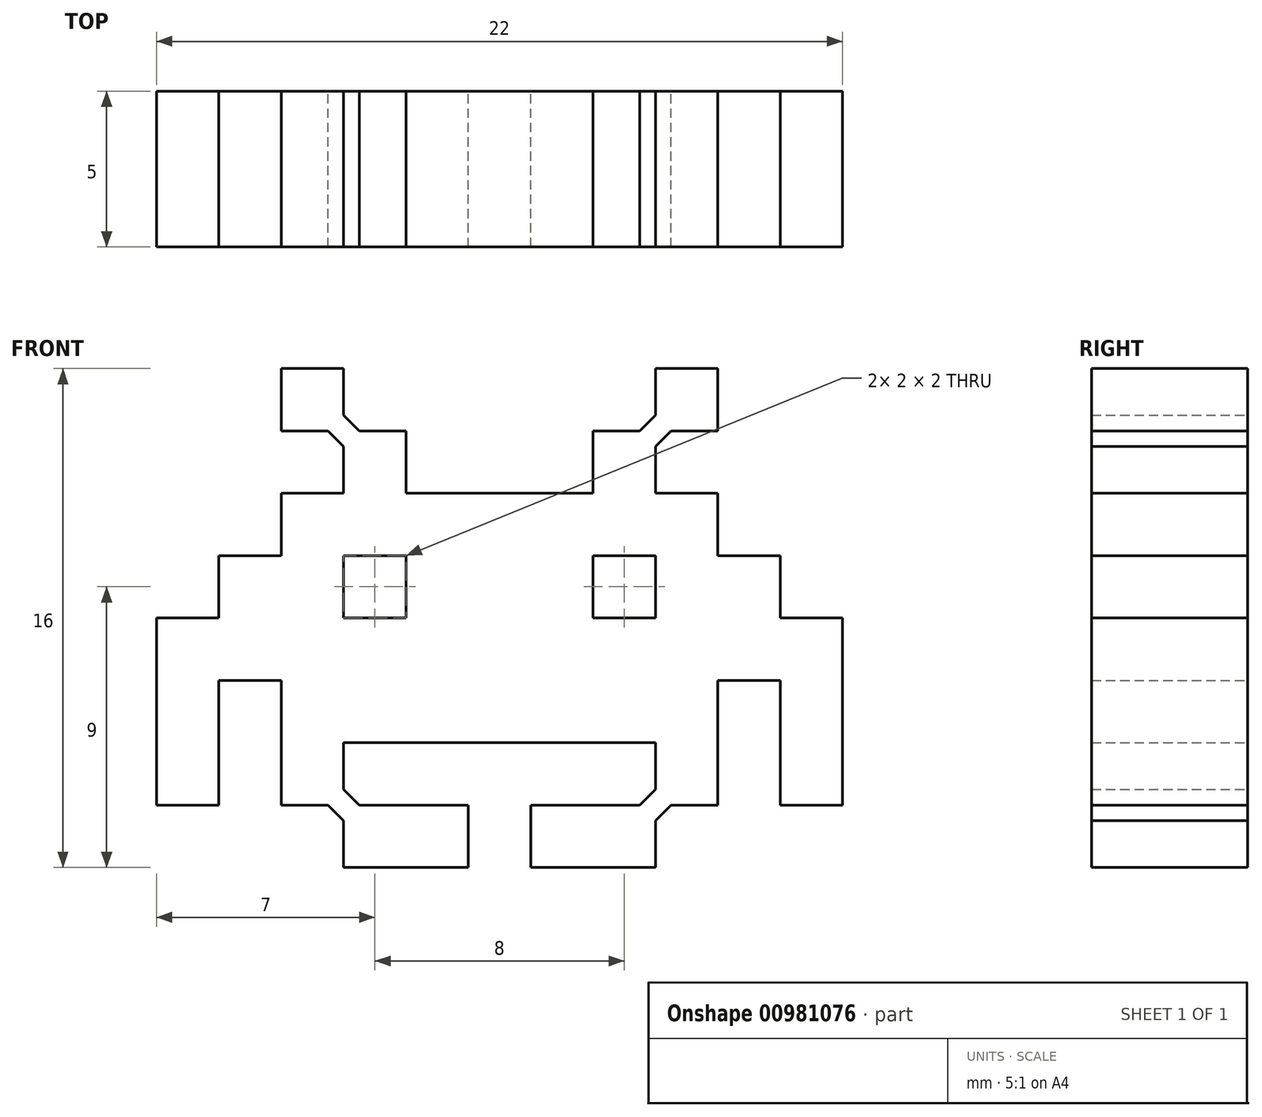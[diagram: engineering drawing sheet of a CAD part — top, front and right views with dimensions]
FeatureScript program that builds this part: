
annotation { "Feature Type Name" : "Feature", "Feature Type Description" : "" }
export const myFeature = defineFeature(function(context is Context, id is Id, definition is map)
    precondition{}
    {
        {
            var Q0;
            Q0=qCreatedBy(makeId("Front.planeOp"),FACE);
            var sketch = newSketch(context, id + "F0", { "sketchPlane" : qUnion([Q0])});
            skLineSegment(sketch, "E0.bottom", {"start": v(1, 1) * mm, "end": v(-1, 1) * mm});
            skLineSegment(sketch, "E0.top", {"start": v(1, -1) * mm, "end": v(-1, -1) * mm});
            skLineSegment(sketch, "E0.left", {"start": v(1, 1) * mm, "end": v(1, -1) * mm});
            skLineSegment(sketch, "E0.right", {"start": v(-1, 1) * mm, "end": v(-1, -1) * mm});
            skPoint(sketch, "E0.middle", {"position": v(0, 0) * mm});
            skPoint(sketch, "E1.1.0.2", {"position": v(2, 0) * mm});
            skLineSegment(sketch, "E1.1.0.3", {"start": v(3, 1) * mm, "end": v(1, 1) * mm});
            skLineSegment(sketch, "E1.2.0.0", {"start": v(5, 1) * mm, "end": v(5, -1) * mm});
            skLineSegment(sketch, "E1.2.0.1", {"start": v(3, 1) * mm, "end": v(3, -1) * mm});
            skPoint(sketch, "E1.2.0.2", {"position": v(4, 0) * mm});
            skLineSegment(sketch, "E1.2.0.3", {"start": v(5, 1) * mm, "end": v(3, 1) * mm});
            skLineSegment(sketch, "E1.3.0.0", {"start": v(7, 1) * mm, "end": v(7, -1) * mm});
            skPoint(sketch, "E1.3.0.2", {"position": v(6, 0) * mm});
            skLineSegment(sketch, "E1.3.0.3", {"start": v(7, 1) * mm, "end": v(5, 1) * mm});
            skPoint(sketch, "E2.MirrorP", {"position": v(-2, 0) * mm});
            skPoint(sketch, "E3.0.1.0", {"position": v(4, 2) * mm});
            skLineSegment(sketch, "E3.0.1.2", {"start": v(5, 3) * mm, "end": v(3, 3) * mm});
            skLineSegment(sketch, "E3.0.1.3", {"start": v(5, 3) * mm, "end": v(5, 1) * mm});
            skLineSegment(sketch, "E3.0.1.4", {"start": v(3, 3) * mm, "end": v(3, 1) * mm});
            skLineSegment(sketch, "E4.2.0.3", {"start": v(7, 3) * mm, "end": v(5, 3) * mm});
            skPoint(sketch, "E5.0.1.0", {"position": v(6, 4) * mm});
            skLineSegment(sketch, "E5.0.1.2", {"start": v(7, 5) * mm, "end": v(5, 5) * mm});
            skLineSegment(sketch, "E5.0.1.3", {"start": v(7, 5) * mm, "end": v(7, 3) * mm});
            skLineSegment(sketch, "E5.0.1.4", {"start": v(5, 5) * mm, "end": v(5, 3) * mm});
            skLineSegment(sketch, "E6.right", {"start": v(-1, -1) * mm, "end": v(-1, -3) * mm});
            skPoint(sketch, "E6.middle", {"position": v(0, -2) * mm});
            skPoint(sketch, "E7.1.0.2", {"position": v(2, -2) * mm});
            skLineSegment(sketch, "E7.1.0.3", {"start": v(3, -1) * mm, "end": v(1, -1) * mm});
            skLineSegment(sketch, "E7.1.0.4", {"start": v(3, -3) * mm, "end": v(1, -3) * mm});
            skLineSegment(sketch, "E7.2.0.0", {"start": v(5, -1) * mm, "end": v(5, -3) * mm});
            skLineSegment(sketch, "E7.2.0.1", {"start": v(3, -1) * mm, "end": v(3, -3) * mm});
            skPoint(sketch, "E7.2.0.2", {"position": v(4, -2) * mm});
            skLineSegment(sketch, "E7.2.0.3", {"start": v(5, -1) * mm, "end": v(3, -1) * mm});
            skLineSegment(sketch, "E7.2.0.4", {"start": v(5, -3) * mm, "end": v(3, -3) * mm});
            skPoint(sketch, "E7.3.0.2", {"position": v(6, -2) * mm});
            skLineSegment(sketch, "E7.3.0.3", {"start": v(7, -1) * mm, "end": v(5, -1) * mm});
            skLineSegment(sketch, "E7.3.0.4", {"start": v(7, -3) * mm, "end": v(5, -3) * mm});
            skLineSegment(sketch, "E8.2.0.3", {"start": v(9, -3) * mm, "end": v(7, -3) * mm});
            skPoint(sketch, "E9.0.1.0", {"position": v(8, -2) * mm});
            skLineSegment(sketch, "E9.0.1.2", {"start": v(9, -1) * mm, "end": v(7, -1) * mm});
            skLineSegment(sketch, "E9.0.1.3", {"start": v(9, -1) * mm, "end": v(9, -3) * mm});
            skLineSegment(sketch, "E9.0.1.4", {"start": v(7, -1) * mm, "end": v(7, -3) * mm});
            skLineSegment(sketch, "E10.left", {"start": v(1, -3) * mm, "end": v(1, -5) * mm});
            skLineSegment(sketch, "E10.right", {"start": v(-1, -3) * mm, "end": v(-1, -5) * mm});
            skPoint(sketch, "E10.middle", {"position": v(0, -4) * mm});
            skPoint(sketch, "E11.1.0.2", {"position": v(2, -4) * mm});
            skLineSegment(sketch, "E11.1.0.4", {"start": v(3, -5) * mm, "end": v(1, -5) * mm});
            skLineSegment(sketch, "E11.2.0.0", {"start": v(5, -3) * mm, "end": v(5, -5) * mm});
            skLineSegment(sketch, "E11.2.0.1", {"start": v(3, -3) * mm, "end": v(3, -5) * mm});
            skPoint(sketch, "E11.2.0.2", {"position": v(4, -4) * mm});
            skLineSegment(sketch, "E11.2.0.4", {"start": v(5, -5) * mm, "end": v(3, -5) * mm});
            skPoint(sketch, "E11.3.0.2", {"position": v(6, -4) * mm});
            skLineSegment(sketch, "E11.3.0.4", {"start": v(7, -5) * mm, "end": v(5, -5) * mm});
            skLineSegment(sketch, "E12.2.0.3", {"start": v(9, -5) * mm, "end": v(7, -5) * mm});
            skPoint(sketch, "E13.0.1.0", {"position": v(8, -4) * mm});
            skLineSegment(sketch, "E13.0.1.3", {"start": v(9, -3) * mm, "end": v(9, -5) * mm});
            skLineSegment(sketch, "E13.0.1.4", {"start": v(7, -3) * mm, "end": v(7, -5) * mm});
            skLineSegment(sketch, "E14.2.0.3", {"start": v(11, -5) * mm, "end": v(9, -5) * mm});
            skPoint(sketch, "E15.0.1.0", {"position": v(10, -4) * mm});
            skLineSegment(sketch, "E15.0.1.3", {"start": v(11, -3) * mm, "end": v(11, -5) * mm});
            skLineSegment(sketch, "E16", {"start": v(9, -3) * mm, "end": v(11, -3) * mm});
            skPoint(sketch, "E17.0.1.0", {"position": v(10, -6) * mm});
            skLineSegment(sketch, "E17.0.1.1", {"start": v(9, -5) * mm, "end": v(9, -7) * mm});
            skLineSegment(sketch, "E17.0.1.4", {"start": v(11, -5) * mm, "end": v(11, -7) * mm});
            skPoint(sketch, "E17.0.2.0", {"position": v(10, -8) * mm});
            skLineSegment(sketch, "E17.0.2.1", {"start": v(9, -7) * mm, "end": v(9, -9) * mm});
            skLineSegment(sketch, "E17.0.2.2", {"start": v(11, -9) * mm, "end": v(9, -9) * mm});
            skLineSegment(sketch, "E17.0.2.3", {"start": v(9, -7) * mm, "end": v(11, -7) * mm});
            skLineSegment(sketch, "E17.0.2.4", {"start": v(11, -7) * mm, "end": v(11, -9) * mm});
            skLineSegment(sketch, "E17.direction1", {"start": v(9, -5) * mm, "end": v(10, -5) * mm, "construction": true});
            skLineSegment(sketch, "E18.top", {"start": v(1, -7) * mm, "end": v(-1, -7) * mm});
            skLineSegment(sketch, "E18.left", {"start": v(1, -5) * mm, "end": v(1, -7) * mm});
            skLineSegment(sketch, "E18.right", {"start": v(-1, -5) * mm, "end": v(-1, -7) * mm});
            skPoint(sketch, "E18.middle", {"position": v(0, -6) * mm});
            skPoint(sketch, "E19.1.0.2", {"position": v(2, -6) * mm});
            skLineSegment(sketch, "E19.1.0.4", {"start": v(3, -7) * mm, "end": v(1, -7) * mm});
            skLineSegment(sketch, "E19.2.0.0", {"start": v(5, -5) * mm, "end": v(5, -7) * mm});
            skLineSegment(sketch, "E19.2.0.1", {"start": v(3, -5) * mm, "end": v(3, -7) * mm});
            skPoint(sketch, "E19.2.0.2", {"position": v(4, -6) * mm});
            skLineSegment(sketch, "E19.2.0.4", {"start": v(5, -7) * mm, "end": v(3, -7) * mm});
            skPoint(sketch, "E19.3.0.2", {"position": v(6, -6) * mm});
            skLineSegment(sketch, "E19.3.0.4", {"start": v(7, -7) * mm, "end": v(5, -7) * mm});
            skLineSegment(sketch, "E20.direction1", {"start": v(3, -7) * mm, "end": v(4, -7) * mm, "construction": true});
            skLineSegment(sketch, "E21.0.1.4", {"start": v(7, -5) * mm, "end": v(7, -7) * mm});
            skLineSegment(sketch, "E22.0.2.1", {"start": v(5, -7) * mm, "end": v(5, -9) * mm});
            skLineSegment(sketch, "E22.0.2.2", {"start": v(5, -9) * mm, "end": v(3, -9) * mm});
            skLineSegment(sketch, "E22.0.2.4", {"start": v(7, -7) * mm, "end": v(7, -9) * mm});
            skLineSegment(sketch, "E23.top", {"start": v(3, -9) * mm, "end": v(1, -9) * mm});
            skLineSegment(sketch, "E24.top", {"start": v(3, -11) * mm, "end": v(1, -11) * mm});
            skLineSegment(sketch, "E24.left", {"start": v(3, -9) * mm, "end": v(3, -11) * mm});
            skLineSegment(sketch, "E24.right", {"start": v(1, -9) * mm, "end": v(1, -11) * mm});
            skPoint(sketch, "E24.middle", {"position": v(2, -10) * mm});
            skPoint(sketch, "E25.1.0.2", {"position": v(4, -10) * mm});
            skLineSegment(sketch, "E25.1.0.4", {"start": v(5, -11) * mm, "end": v(3, -11) * mm});
            skLineSegment(sketch, "E25.2.0.1", {"start": v(5, -9) * mm, "end": v(5, -11) * mm});
            skLineSegment(sketch, "E26", {"start": v(5, -9) * mm, "end": v(7, -9) * mm});
            skLineSegment(sketch, "E27.MirrorCS", {"start": v(-7, -3) * mm, "end": v(-5, -3) * mm});
            skLineSegment(sketch, "E28.MirrorCS", {"start": v(-11, -5) * mm, "end": v(-9, -5) * mm});
            skLineSegment(sketch, "E29.MirrorCS", {"start": v(-5, -9) * mm, "end": v(-5, -9.5) * mm});
            skPoint(sketch, "E30.MirrorP", {"position": v(-4, 0) * mm});
            skLineSegment(sketch, "E31.MirrorCS", {"start": v(-5, -7) * mm, "end": v(-3, -7) * mm});
            skLineSegment(sketch, "E32.MirrorCS", {"start": v(-1, -3) * mm, "end": v(1, -3) * mm});
            skLineSegment(sketch, "E33.MirrorCS", {"start": v(-3, -3) * mm, "end": v(-1, -3) * mm});
            skLineSegment(sketch, "E34.MirrorCS", {"start": v(-9, -5) * mm, "end": v(-10, -5) * mm, "construction": true});
            skLineSegment(sketch, "E35.MirrorCS", {"start": v(-5, -3) * mm, "end": v(-3, -3) * mm});
            skLineSegment(sketch, "E36.MirrorCS", {"start": v(-5, -5) * mm, "end": v(-5, -7) * mm});
            skLineSegment(sketch, "E37.MirrorCS", {"start": v(-5, -1) * mm, "end": v(-5, -3) * mm});
            skLineSegment(sketch, "E38.MirrorCS", {"start": v(-5, -3) * mm, "end": v(-5, -5) * mm});
            skLineSegment(sketch, "E39.MirrorCS", {"start": v(-9, -3) * mm, "end": v(-7, -3) * mm});
            skLineSegment(sketch, "E40.MirrorCS", {"start": v(-3, -7) * mm, "end": v(-4, -7) * mm, "construction": true});
            skLineSegment(sketch, "E41.MirrorCS", {"start": v(-5, 1) * mm, "end": v(-5, -1) * mm});
            skLineSegment(sketch, "E42.MirrorCS", {"start": v(-9, -3) * mm, "end": v(-9, -5) * mm});
            skLineSegment(sketch, "E43.MirrorCS", {"start": v(-11, -5) * mm, "end": v(-11, -7) * mm});
            skLineSegment(sketch, "E44.MirrorCS", {"start": v(-3, -9) * mm, "end": v(-1, -9) * mm});
            skLineSegment(sketch, "E45.MirrorCS", {"start": v(-3, 1) * mm, "end": v(-1, 1) * mm});
            skLineSegment(sketch, "E46.MirrorCS", {"start": v(-3, -3) * mm, "end": v(-3, -5) * mm});
            skPoint(sketch, "E47.MirrorP", {"position": v(-2, -4) * mm});
            skLineSegment(sketch, "E48.MirrorCS", {"start": v(-7, -3) * mm, "end": v(-7, -5) * mm});
            skLineSegment(sketch, "E49.MirrorCS", {"start": v(-7, -1) * mm, "end": v(-5, -1) * mm});
            skPoint(sketch, "E50.MirrorP", {"position": v(-4, -4) * mm});
            skPoint(sketch, "E51.MirrorP", {"position": v(-6, -2) * mm});
            skLineSegment(sketch, "E52.MirrorCS", {"start": v(-5, -9) * mm, "end": v(-5.5, -9) * mm});
            skPoint(sketch, "E53.MirrorP", {"position": v(-2, -10) * mm});
            skPoint(sketch, "E54.MirrorP", {"position": v(-2, -6) * mm});
            skLineSegment(sketch, "E55.MirrorCS", {"start": v(-5, 3) * mm, "end": v(-4.5, 3) * mm});
            skLineSegment(sketch, "E56.MirrorCS", {"start": v(1, -1) * mm, "end": v(1, -3) * mm});
            skLineSegment(sketch, "E57.MirrorCS", {"start": v(-7, -1) * mm, "end": v(-7, -3) * mm});
            skLineSegment(sketch, "E58.MirrorCS", {"start": v(-5, -5) * mm, "end": v(-3, -5) * mm});
            skPoint(sketch, "E59.MirrorP", {"position": v(-8, -2) * mm});
            skLineSegment(sketch, "E60.MirrorCS", {"start": v(-7, -7) * mm, "end": v(-5, -7) * mm});
            skPoint(sketch, "E61.MirrorP", {"position": v(-10, -8) * mm});
            skPoint(sketch, "E62.MirrorP", {"position": v(-8, -4) * mm});
            skLineSegment(sketch, "E63.MirrorCS", {"start": v(-3, -5) * mm, "end": v(-1, -5) * mm});
            skLineSegment(sketch, "E64.MirrorCS", {"start": v(-7, 1) * mm, "end": v(-5, 1) * mm});
            skLineSegment(sketch, "E65.MirrorCS", {"start": v(-9, -7) * mm, "end": v(-11, -7) * mm});
            skLineSegment(sketch, "E66.MirrorCS", {"start": v(-3, 3) * mm, "end": v(-3, 1) * mm});
            skLineSegment(sketch, "E67.MirrorCS", {"start": v(-3, -5) * mm, "end": v(-3, -7) * mm});
            skPoint(sketch, "E68.MirrorP", {"position": v(-6, -4) * mm});
            skLineSegment(sketch, "E69.MirrorCS", {"start": v(-7, -7) * mm, "end": v(-7, -9) * mm});
            skLineSegment(sketch, "E70.MirrorCS", {"start": v(-3, -9) * mm, "end": v(-3, -11) * mm});
            skLineSegment(sketch, "E71.MirrorCS", {"start": v(-9, -1) * mm, "end": v(-7, -1) * mm});
            skLineSegment(sketch, "E72.MirrorCS", {"start": v(-9, -5) * mm, "end": v(-9, -7) * mm});
            skLineSegment(sketch, "E73.MirrorCS", {"start": v(-1, -9) * mm, "end": v(-1, -11) * mm});
            skLineSegment(sketch, "E74.MirrorCS", {"start": v(-9, -1) * mm, "end": v(-9, -3) * mm});
            skLineSegment(sketch, "E75.MirrorCS", {"start": v(-11, -3) * mm, "end": v(-11, -5) * mm});
            skLineSegment(sketch, "E76.MirrorCS", {"start": v(-3, -11) * mm, "end": v(-1, -11) * mm});
            skLineSegment(sketch, "E77.MirrorCS", {"start": v(-3, -7) * mm, "end": v(-1, -7) * mm});
            skLineSegment(sketch, "E78.MirrorCS", {"start": v(-5, -1) * mm, "end": v(-3, -1) * mm});
            skPoint(sketch, "E79.MirrorP", {"position": v(-6, -6) * mm});
            skLineSegment(sketch, "E80.MirrorCS", {"start": v(-7, 5) * mm, "end": v(-5, 5) * mm});
            skLineSegment(sketch, "E81.MirrorCS", {"start": v(-11, -9) * mm, "end": v(-9, -9) * mm});
            skLineSegment(sketch, "E82.MirrorCS", {"start": v(-9, -3) * mm, "end": v(-11, -3) * mm});
            skLineSegment(sketch, "E83.MirrorCS", {"start": v(-1, -5) * mm, "end": v(1, -5) * mm});
            skLineSegment(sketch, "E84.MirrorCS", {"start": v(-7, 5) * mm, "end": v(-7, 3) * mm});
            skLineSegment(sketch, "E85.MirrorCS", {"start": v(-11, -7) * mm, "end": v(-11, -9) * mm});
            skPoint(sketch, "E86.MirrorP", {"position": v(-2, -2) * mm});
            skPoint(sketch, "E87.MirrorP", {"position": v(-10, -6) * mm});
            skLineSegment(sketch, "E88.MirrorCS", {"start": v(-5, -11) * mm, "end": v(-3, -11) * mm});
            skLineSegment(sketch, "E89.MirrorCS", {"start": v(-7, -5) * mm, "end": v(-5, -5) * mm});
            skLineSegment(sketch, "E90.MirrorCS", {"start": v(-9, -5) * mm, "end": v(-7, -5) * mm});
            skLineSegment(sketch, "E91.MirrorCS", {"start": v(-5, 5) * mm, "end": v(-5, 4) * mm});
            skPoint(sketch, "E92.MirrorP", {"position": v(-4, -10) * mm});
            skLineSegment(sketch, "E93.MirrorCS", {"start": v(-5, -7) * mm, "end": v(-5, -8) * mm});
            skLineSegment(sketch, "E94.MirrorCS", {"start": v(-5, 3) * mm, "end": v(-5, 2.5) * mm});
            skPoint(sketch, "E95.MirrorP", {"position": v(-6, 4) * mm});
            skLineSegment(sketch, "E96.MirrorCS", {"start": v(-9, -7) * mm, "end": v(-9, -9) * mm});
            skLineSegment(sketch, "E97.MirrorCS", {"start": v(-5, 1) * mm, "end": v(-3, 1) * mm});
            skPoint(sketch, "E98.MirrorP", {"position": v(-10, -4) * mm});
            skLineSegment(sketch, "E99.MirrorCS", {"start": v(-3, -1) * mm, "end": v(-1, -1) * mm});
            skLineSegment(sketch, "E100.MirrorCS", {"start": v(-7, -5) * mm, "end": v(-7, -7) * mm});
            skPoint(sketch, "E101.MirrorP", {"position": v(-4, -2) * mm});
            skLineSegment(sketch, "E102.MirrorCS", {"start": v(-3, 1) * mm, "end": v(-3, -1) * mm});
            skPoint(sketch, "E103.MirrorP", {"position": v(-4, -6) * mm});
            skPoint(sketch, "E104.MirrorP", {"position": v(-6, 0) * mm});
            skLineSegment(sketch, "E105.MirrorCS", {"start": v(-7, 1) * mm, "end": v(-7, -1) * mm});
            skLineSegment(sketch, "E106.MirrorCS", {"start": v(-5, -9) * mm, "end": v(-4.5, -9) * mm});
            skLineSegment(sketch, "E107.MirrorCS", {"start": v(-3, -1) * mm, "end": v(-3, -3) * mm});
            skPoint(sketch, "E108.MirrorP", {"position": v(-4, 2) * mm});
            skLineSegment(sketch, "E109.MirrorCS", {"start": v(-7, 3) * mm, "end": v(-6, 3) * mm});
            skLineSegment(sketch, "E110", {"start": v(-6, 3) * mm, "end": v(-5.5, 3) * mm});
            skLineSegment(sketch, "E111", {"start": v(-5, 2) * mm, "end": v(-5, 1) * mm});
            skLineSegment(sketch, "E112", {"start": v(-5, 2.5) * mm, "end": v(-5, 2) * mm});
            skLineSegment(sketch, "E113", {"start": v(-5.5, 3) * mm, "end": v(-5, 3) * mm});
            skLineSegment(sketch, "E114", {"start": v(-5, 4) * mm, "end": v(-5, 3.5) * mm});
            skLineSegment(sketch, "E115", {"start": v(-5, 3.5) * mm, "end": v(-5, 3) * mm});
            skLineSegment(sketch, "E116", {"start": v(-4, 3) * mm, "end": v(-3, 3) * mm});
            skLineSegment(sketch, "E117", {"start": v(-4.5, 3) * mm, "end": v(-4, 3) * mm});
            skLineSegment(sketch, "E118", {"start": v(-5.5, 3) * mm, "end": v(-5, 2.5) * mm});
            skLineSegment(sketch, "E119", {"start": v(-5, 3.5) * mm, "end": v(-4.5, 3) * mm});
            skLineSegment(sketch, "E120.MirrorCS", {"start": v(5, 3.5) * mm, "end": v(4.5, 3) * mm});
            skLineSegment(sketch, "E121.MirrorCS", {"start": v(5.5, 3) * mm, "end": v(5, 2.5) * mm});
            skLineSegment(sketch, "E122", {"start": v(-6, -9) * mm, "end": v(-7, -9) * mm});
            skLineSegment(sketch, "E123", {"start": v(-5, -8) * mm, "end": v(-5, -8.5) * mm});
            skLineSegment(sketch, "E124", {"start": v(-4, -9) * mm, "end": v(-3, -9) * mm});
            skLineSegment(sketch, "E125", {"start": v(-5, -10) * mm, "end": v(-5, -11) * mm});
            skLineSegment(sketch, "E126", {"start": v(-5.5, -9) * mm, "end": v(-6, -9) * mm});
            skLineSegment(sketch, "E127", {"start": v(-5, -8.5) * mm, "end": v(-5, -9) * mm});
            skLineSegment(sketch, "E128", {"start": v(-4.5, -9) * mm, "end": v(-4, -9) * mm});
            skLineSegment(sketch, "E129", {"start": v(-5, -9.5) * mm, "end": v(-5, -10) * mm});
            skLineSegment(sketch, "E130", {"start": v(-5.5, -9) * mm, "end": v(-5, -9.5) * mm});
            skLineSegment(sketch, "E131", {"start": v(-5, -8.5) * mm, "end": v(-4.5, -9) * mm});
            skLineSegment(sketch, "E132.MirrorCS", {"start": v(5, -8.5) * mm, "end": v(4.5, -9) * mm});
            skLineSegment(sketch, "E133.MirrorCS", {"start": v(5.5, -9) * mm, "end": v(5, -9.5) * mm});
            skSolve(sketch);
        }
        {
            var Q0;
            Q0 = qSketchRegion(id + "F0", true);
            var Q1;
            Q1=makeQuery(id+"F0.imprint","IMPRINT",FACE,{"disambiguationData":[TD([[makeQuery(id+"F0.imprint","IMPRINT",EDGE,{"derivedFrom":sQuery(id+"F0.wireOp",EDGE,"E6.right")}),-1.0]])]});
            var Q2;
            Q2=makeQuery(id+"F0.imprint","IMPRINT",FACE,{"disambiguationData":[TD([[makeQuery(id+"F0.imprint","IMPRINT",EDGE,{"derivedFrom":sQuery(id+"F0.wireOp",EDGE,"E35.MirrorCS")}),-1.0]])]});
            var Q3;
            Q3=makeQuery(id+"F0.imprint","IMPRINT",FACE,{"disambiguationData":[TD([[makeQuery(id+"F0.imprint","IMPRINT",EDGE,{"derivedFrom":sQuery(id+"F0.wireOp",EDGE,"E10.right")}),-1.0]])]});
            var Q4;
            Q4=makeQuery(id+"F0.imprint","IMPRINT",FACE,{"disambiguationData":[TD([[makeQuery(id+"F0.imprint","IMPRINT",EDGE,{"derivedFrom":sQuery(id+"F0.wireOp",EDGE,"E10.left")}),-1.0]])]});
            var Q5;
            Q5=makeQuery(id+"F0.imprint","IMPRINT",FACE,{"disambiguationData":[TD([[makeQuery(id+"F0.imprint","IMPRINT",EDGE,{"derivedFrom":sQuery(id+"F0.wireOp",EDGE,"E0.top")}),1.0]])]});
            var Q6;
            Q6=makeQuery(id+"F0.imprint","IMPRINT",FACE,{"disambiguationData":[TD([[makeQuery(id+"F0.imprint","IMPRINT",EDGE,{"derivedFrom":sQuery(id+"F0.wireOp",EDGE,"E7.2.0.4")}),1.0]])]});
            var Q7;
            Q7=makeQuery(id+"F0.imprint","IMPRINT",FACE,{"disambiguationData":[TD([[makeQuery(id+"F0.imprint","IMPRINT",EDGE,{"derivedFrom":sQuery(id+"F0.wireOp",EDGE,"E7.1.0.4")}),1.0]])]});
            var Q8;
            Q8=makeQuery(id+"F0.imprint","IMPRINT",FACE,{"disambiguationData":[TD([[makeQuery(id+"F0.imprint","IMPRINT",EDGE,{"derivedFrom":sQuery(id+"F0.wireOp",EDGE,"E7.1.0.3")}),1.0]])]});
            extrude(context, id + "F1", {"entities" : qUnion([Q0, Q1, Q2, Q3, Q4, Q5, Q6, Q7, Q8]), "depth" : 5 * mm, "offsetDistance" : 25 * mm});
        }
    });
